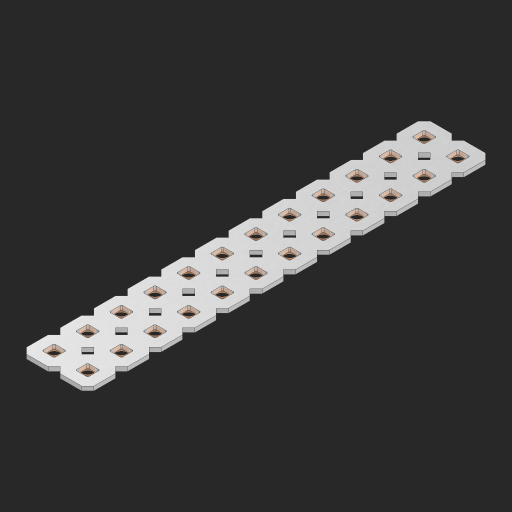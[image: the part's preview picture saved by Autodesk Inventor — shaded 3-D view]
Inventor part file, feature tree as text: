
AUTODESK INVENTOR PART (.ipt)
format: ipt  version: 2023 (Build 270158000, 158)  size: 551,936 bytes
history: native  units: in
note: dims shown in document units (in); Inventor stores cm internally (conversion verified against a paired STEP export)
features: other x25, extrude x23, sketch x2, pattern_linear x1
ambient origin geometry x8: Origin, YZ Plane, XZ Plane, XY Plane, X Axis, Y Axis, Z Axis, Center Point
bodies: Solid1 (feature_tree), Body (feature_tree)
feature tree (51):
  pattern_linear  "Rectangular Pattern1"  Spacing1=0.09in  [1 undecoded]
  sketch  "Sketch1"  dims[d1=0.5in]
  sketch  "Sketch2"  dims[d2=0.182in d3=0.09in d4=0.09in d5=0.09in d6=0.09in d7=0.09in d8=0.09in d9=0.09in d10=0.09in d11=0.02in d13=0.0in d14=0.172in d15=0.0625in d16=0.0in d19=0.5in d22=0.5in]
  other  "Srf1"
  other  "Srf126"
  other  "Srf127"
  other  "Srf128"
  other  "Srf129"
  other  "Srf130"
  other  "Srf131"
  other  "Srf250"
  other  "Srf251"
  other  "Srf252"
  other  "Srf253"
  other  "Srf254"
  other  "Srf268"
  other  "Srf269"
  other  "Srf270"
  other  "Srf271"
  other  "Srf272"
  other  "Srf273"
  other  "Srf274"
  other  "Srf275"
  other  "Srf276"
  other  "Srf277"
  other  "Srf278"
  other  "Srf279"
  other  "Circle"
  extrude  "ExtrusionSrf126"  Depth=0.09in
  extrude  "ExtrusionSrf127"  Depth=0.09in
  extrude  "ExtrusionSrf128"  Depth=0.09in
  extrude  "ExtrusionSrf129"  Depth=0.09in
  extrude  "ExtrusionSrf130"  Depth=0.09in
  extrude  "ExtrusionSrf131"  Depth=0.09in
  extrude  "ExtrusionSrf250"  Depth=0.09in
  extrude  "ExtrusionSrf251"  Depth=0.02in
  extrude  "ExtrusionSrf252"  TaperAngle=0.0deg  [1 undecoded]
  extrude  "ExtrusionSrf253"  Depth=0.5in
  extrude  "ExtrusionSrf254"  Depth=0.0625in TaperAngle=0.0deg
  extrude  "ExtrusionSrf268"  Depth=0.5in
  extrude  "ExtrusionSrf269"  Depth=0.5in
  extrude  "ExtrusionSrf270"  [1 undecoded]
  extrude  "ExtrusionSrf271"  [1 undecoded]
  extrude  "ExtrusionSrf272"  [1 undecoded]
  extrude  "ExtrusionSrf273"  [1 undecoded]
  extrude  "ExtrusionSrf274"  [1 undecoded]
  extrude  "ExtrusionSrf275"  [1 undecoded]
  extrude  "ExtrusionSrf276"  [1 undecoded]
  extrude  "ExtrusionSrf277"  [1 undecoded]
  extrude  "ExtrusionSrf278"  [1 undecoded]
  extrude  "ExtrusionSrf279"  [1 undecoded]
note: 12 required parameter values undecoded (feature->parameter linkage not recoverable at this tier; creation-order binding heuristic only, values carry confidence <= 0.55)
